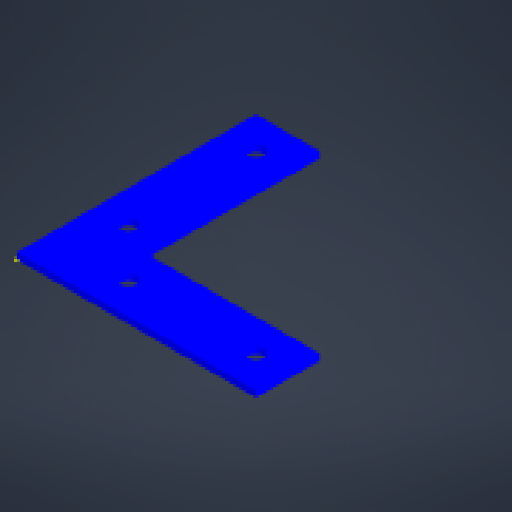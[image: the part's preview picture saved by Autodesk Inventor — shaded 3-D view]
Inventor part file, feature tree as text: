
AUTODESK INVENTOR PART (.ipt)
format: ipt  version: 2024 (Build 280153000, 153)  size: 214,016 bytes
history: native  units: mm
features: extrude x2, sketch x2, other x1
ambient origin geometry x8: Origin, YZ Plane, XZ Plane, XY Plane, X Axis, Y Axis, Z Axis, Center Point
bodies: Body1 (feature_tree)
feature tree (5):
  other  "Твердое тело1"
  extrude  "Выдавливание1"  Depth=5.0mm
  extrude  "Выдавливание2"  Depth=2.0mm TaperAngle=0.0deg
  sketch  "Эскиз1"
  sketch  "Эскиз2"
